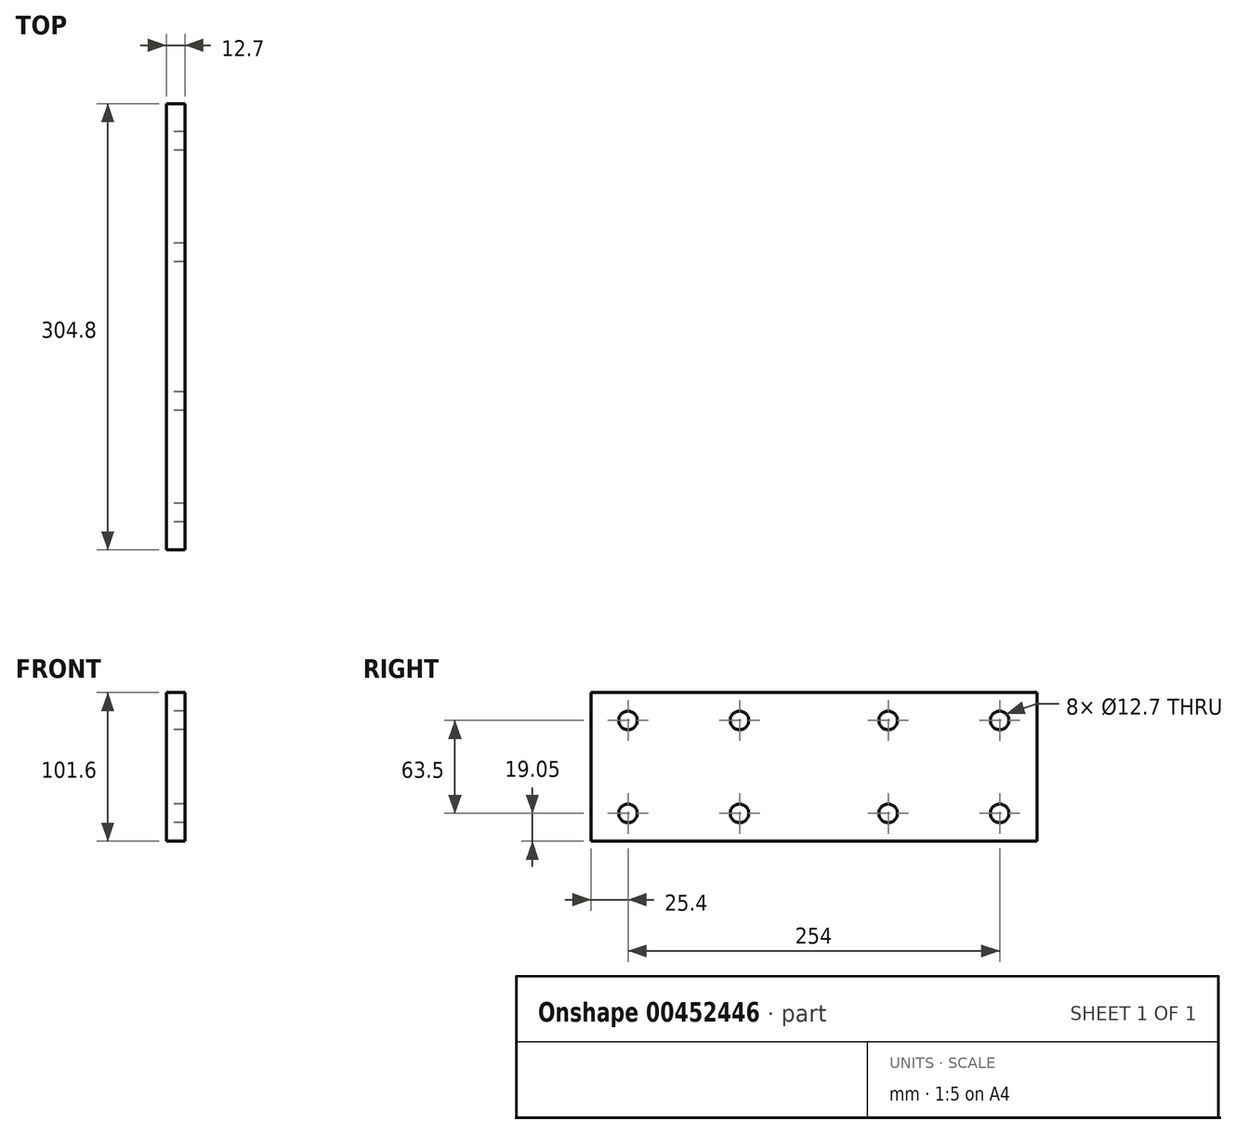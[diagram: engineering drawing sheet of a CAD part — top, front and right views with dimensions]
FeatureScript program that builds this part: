
annotation { "Feature Type Name" : "Feature", "Feature Type Description" : "" }
export const myFeature = defineFeature(function(context is Context, id is Id, definition is map)
    precondition{}
    {
        {
            var Q0;
            Q0=qCreatedBy(makeId("Right.planeOp"),FACE);
            var sketch = newSketch(context, id + "F0", { "sketchPlane" : qUnion([Q0])});
            skLineSegment(sketch, "E0.bottom", {"start": v(-152.4, 50.8) * mm, "end": v(152.4, 50.8) * mm});
            skLineSegment(sketch, "E0.top", {"start": v(-152.4, -50.8) * mm, "end": v(152.4, -50.8) * mm});
            skLineSegment(sketch, "E0.left", {"start": v(-152.4, 50.8) * mm, "end": v(-152.4, -50.8) * mm});
            skLineSegment(sketch, "E0.right", {"start": v(152.4, 50.8) * mm, "end": v(152.4, -50.8) * mm});
            skSolve(sketch);
        }
        {
            var Q0;
            Q0=makeQuery(id+"F0.imprint","IMPRINT",FACE,{"disambiguationData":[TD([[makeQuery(id+"F0.imprint","IMPRINT",EDGE,{"derivedFrom":sQuery(id+"F0.wireOp",EDGE,"E0.bottom")}),-1.0]])]});
            extrude(context, id + "F1", {"entities" : qUnion([Q0]), "depth" : 6.35 * mm, "hasSecondDirection" : true, "secondDirectionOppositeDirection" : true, "secondDirectionDepth" : 6.35 * mm});
        }
        {
            var Q0;
            Q0=makeQuery(id+"F1.opExtrude","CAP_FACE",FACE,{"disambiguationData":[OSD([sQuery(id+"F0.wireOp",EDGE,"E0.bottom"),sQuery(id+"F0.wireOp",EDGE,"E0.top"),sQuery(id+"F0.wireOp",EDGE,"E0.left"),sQuery(id+"F0.wireOp",EDGE,"E0.right")])],"isStart":false});
            var sketch = newSketch(context, id + "F2", { "sketchPlane" : qUnion([Q0])});
            skLineSegment(sketch, "E1.bottom", {"start": v(-127, 31.75) * mm, "end": v(-50.8, 31.75) * mm, "construction": true});
            skLineSegment(sketch, "E1.top", {"start": v(-127, -31.75) * mm, "end": v(-50.8, -31.75) * mm, "construction": true});
            skLineSegment(sketch, "E1.left", {"start": v(-127, 31.75) * mm, "end": v(-127, -31.75) * mm, "construction": true});
            skLineSegment(sketch, "E1.right", {"start": v(-50.8, 31.75) * mm, "end": v(-50.8, -31.75) * mm, "construction": true});
            skLineSegment(sketch, "E2", {"start": v(0, 50.8) * mm, "end": v(0, -50.8) * mm, "construction": true});
            skLineSegment(sketch, "E3", {"start": v(-152.4, 0) * mm, "end": v(152.4, 0) * mm, "construction": true});
            skLineSegment(sketch, "E4.MirrorCS", {"start": v(50.8, 31.75) * mm, "end": v(50.8, -31.75) * mm, "construction": true});
            skLineSegment(sketch, "E5.MirrorCS", {"start": v(127, 31.75) * mm, "end": v(127, -31.75) * mm, "construction": true});
            skLineSegment(sketch, "E6.MirrorCS", {"start": v(127, -31.75) * mm, "end": v(50.8, -31.75) * mm, "construction": true});
            skLineSegment(sketch, "E7.MirrorCS", {"start": v(127, 31.75) * mm, "end": v(50.8, 31.75) * mm, "construction": true});
            skSolve(sketch);
        }
        {
            var Q0;
            Q0=sQuery(id+"F2.wireOp",VERTEX,"E1.left.start");
            var Q1;
            Q1=sQuery(id+"F2.wireOp",VERTEX,"E1.left.end");
            var Q2;
            Q2=sQuery(id+"F2.wireOp",VERTEX,"E1.top.end");
            var Q3;
            Q3=sQuery(id+"F2.wireOp",VERTEX,"E1.right.start");
            var Q4;
            Q4=sQuery(id+"F2.wireOp",VERTEX,"E7.MirrorCS.end");
            var Q5;
            Q5=sQuery(id+"F2.wireOp",VERTEX,"E5.MirrorCS.start");
            var Q6;
            Q6=sQuery(id+"F2.wireOp",VERTEX,"E6.MirrorCS.start");
            var Q7;
            Q7=sQuery(id+"F2.wireOp",VERTEX,"E6.MirrorCS.end");
            var Q8;
            Q8=makeQuery(id+"F1.opExtrude","SWEPT_BODY",BODY,{"disambiguationData":[OSD([sQuery(id+"F0.wireOp",EDGE,"E0.bottom"),sQuery(id+"F0.wireOp",EDGE,"E0.top"),sQuery(id+"F0.wireOp",EDGE,"E0.left"),sQuery(id+"F0.wireOp",EDGE,"E0.right")])]});
            hole(context, id + "F3", {"style" : HoleStyle.SIMPLE, "endStyle" : HoleEndStyle.THROUGH, "holeDiameter" : 12.7 * mm, "majorDiameter" : 6.35 * mm, "isTappedThrough" : true, "tappedDepth" : 12.7 * mm, "tapClearance" : 3, "locations" : qUnion([Q0, Q1, Q2, Q3, Q4, Q5, Q6, Q7]), "scope" : qUnion([Q8])});
        }
    });
